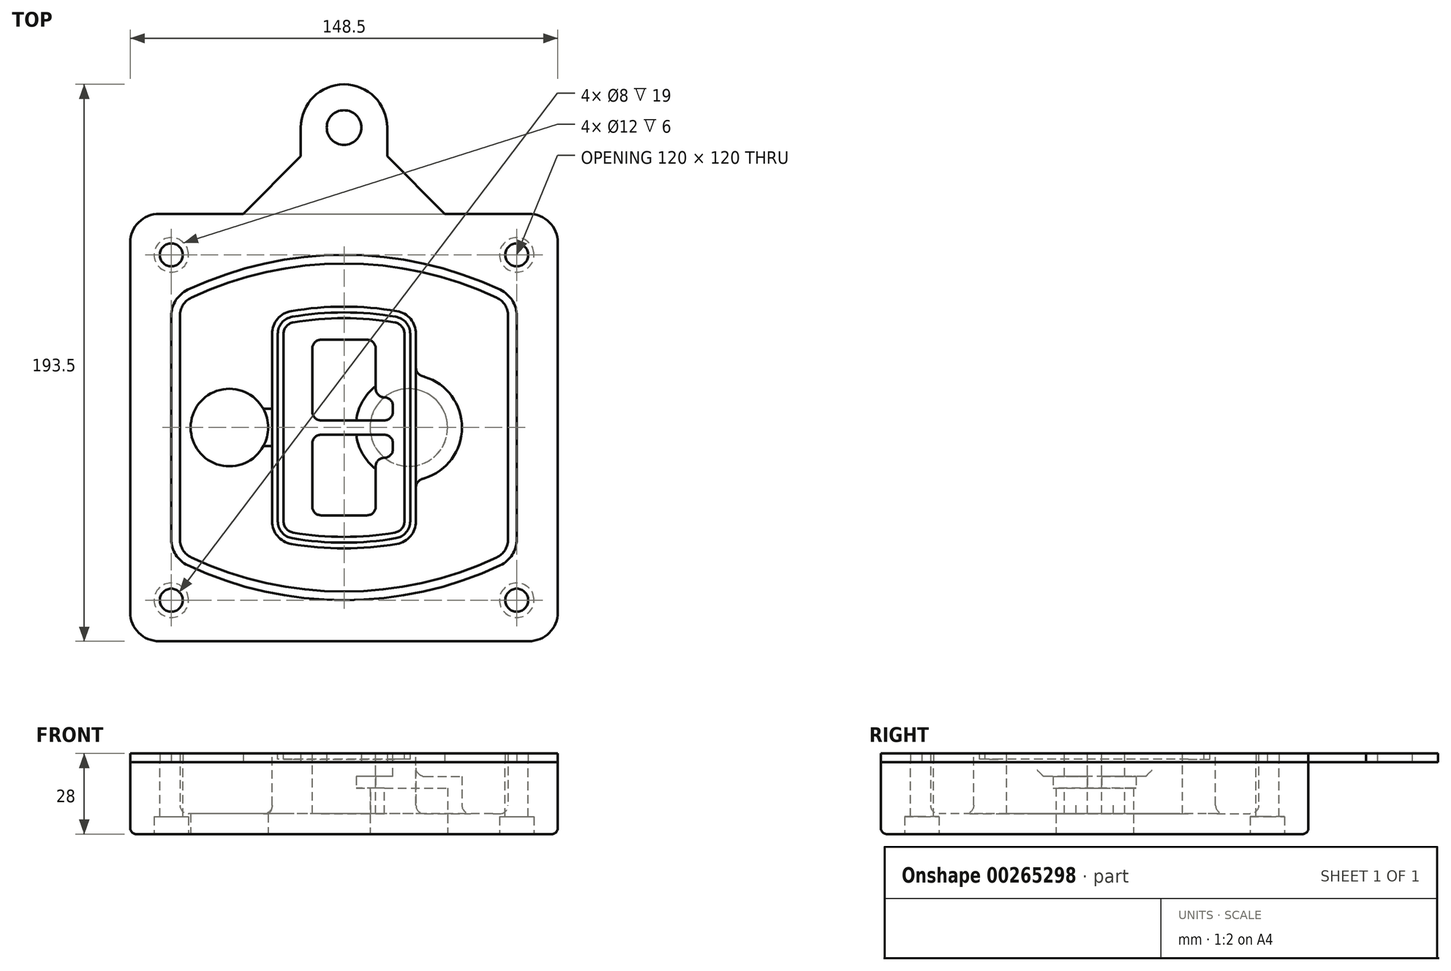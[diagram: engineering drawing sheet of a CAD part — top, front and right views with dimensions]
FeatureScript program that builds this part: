
annotation { "Feature Type Name" : "Feature", "Feature Type Description" : "" }
export const myFeature = defineFeature(function(context is Context, id is Id, definition is map)
    precondition{}
    {
        {
            var Q0;
            Q0=qCreatedBy(makeId("Top.planeOp"),FACE);
            var sketch = newSketch(context, id + "F0", { "sketchPlane" : qUnion([Q0])});
            skPoint(sketch, "E0.rect.middle", {"position": v(0, 0) * mm});
            skLineSegment(sketch, "E1.bottom", {"start": v(-64.25, -74.25) * mm, "end": v(64.25, -74.25) * mm});
            skLineSegment(sketch, "E1.top", {"start": v(-64.25, 74.25) * mm, "end": v(64.25, 74.25) * mm});
            skLineSegment(sketch, "E1.left", {"start": v(-74.25, -64.25) * mm, "end": v(-74.25, 64.25) * mm});
            skLineSegment(sketch, "E1.right", {"start": v(74.25, -64.25) * mm, "end": v(74.25, 64.25) * mm});
            skLineSegment(sketch, "E2", {"start": v(-74.25, 74.25) * mm, "end": v(74.25, -74.25) * mm, "construction": true});
            skLineSegment(sketch, "E3", {"start": v(74.25, 74.25) * mm, "end": v(-74.25, -74.25) * mm, "construction": true});
            skCircle(sketch, "E4", {"center": v(-60, 60) * mm, "radius": 4 * mm});
            skCircle(sketch, "E5", {"center": v(60, 60) * mm, "radius": 4 * mm});
            skCircle(sketch, "E6", {"center": v(60, -60) * mm, "radius": 4 * mm});
            skCircle(sketch, "E7", {"center": v(-60, -60) * mm, "radius": 4 * mm});
            skLineSegment(sketch, "E8", {"start": v(-60, 60) * mm, "end": v(60, 60) * mm, "construction": true});
            skLineSegment(sketch, "E9", {"start": v(60, 60) * mm, "end": v(60, -60) * mm, "construction": true});
            skLineSegment(sketch, "E10", {"start": v(60, -60) * mm, "end": v(-60, -60) * mm, "construction": true});
            skLineSegment(sketch, "E11", {"start": v(-60, -60) * mm, "end": v(-60, 60) * mm, "construction": true});
            skLineSegment(sketch, "E12", {"start": v(-60, 38.83) * mm, "end": v(-60, -38.83) * mm});
            skLineSegment(sketch, "E13", {"start": v(60, 38.83) * mm, "end": v(60, -38.83) * mm});
            skArc(sketch, "E14", {"start": v(54.26, 47.88) * mm, "mid": v(0, 60) * mm, "end": v(-54.26, 47.88) * mm});
            skArc(sketch, "E15", {"start": v(-54.26, -47.88) * mm, "mid": v(0, -60) * mm, "end": v(54.26, -47.88) * mm});
            skLineSegment(sketch, "E16", {"start": v(-60, 0) * mm, "end": v(60, 0) * mm, "construction": true});
            skPoint(sketch, "E17.visualSharp", {"position": v(-60, -45) * mm});
            skArc(sketch, "E17.filletArc", {"start": v(-60, -38.83) * mm, "mid": v(-58.44, -44.2) * mm, "end": v(-54.26, -47.88) * mm});
            skPoint(sketch, "E18.visualSharp", {"position": v(-60, 45) * mm});
            skArc(sketch, "E18.filletArc", {"start": v(-54.26, 47.88) * mm, "mid": v(-58.44, 44.2) * mm, "end": v(-60, 38.83) * mm});
            skPoint(sketch, "E19.visualSharp", {"position": v(60, 45) * mm});
            skArc(sketch, "E19.filletArc", {"start": v(60, 38.83) * mm, "mid": v(58.44, 44.2) * mm, "end": v(54.26, 47.88) * mm});
            skPoint(sketch, "E20.visualSharp", {"position": v(60, -45) * mm});
            skArc(sketch, "E20.filletArc", {"start": v(54.26, -47.88) * mm, "mid": v(58.44, -44.2) * mm, "end": v(60, -38.83) * mm});
            skPoint(sketch, "E21.visualSharp", {"position": v(-74.25, 74.25) * mm});
            skArc(sketch, "E21.filletArc", {"start": v(-64.25, 74.25) * mm, "mid": v(-71.32, 71.32) * mm, "end": v(-74.25, 64.25) * mm});
            skPoint(sketch, "E22.visualSharp", {"position": v(74.25, 74.25) * mm});
            skArc(sketch, "E22.filletArc", {"start": v(74.25, 64.25) * mm, "mid": v(71.32, 71.32) * mm, "end": v(64.25, 74.25) * mm});
            skPoint(sketch, "E23.visualSharp", {"position": v(74.25, -74.25) * mm});
            skArc(sketch, "E23.filletArc", {"start": v(64.25, -74.25) * mm, "mid": v(71.32, -71.32) * mm, "end": v(74.25, -64.25) * mm});
            skPoint(sketch, "E24.visualSharp", {"position": v(-74.25, -74.25) * mm});
            skArc(sketch, "E24.filletArc", {"start": v(-74.25, -64.25) * mm, "mid": v(-71.32, -71.32) * mm, "end": v(-64.25, -74.25) * mm});
            skArc(sketch, "E25.0", {"start": v(57, 38.83) * mm, "mid": v(55.9, 42.58) * mm, "end": v(52.98, 45.17) * mm});
            skLineSegment(sketch, "E25.1", {"start": v(57, 38.83) * mm, "end": v(57, -38.83) * mm});
            skArc(sketch, "E25.2", {"start": v(52.98, -45.17) * mm, "mid": v(55.9, -42.58) * mm, "end": v(57, -38.83) * mm});
            skArc(sketch, "E25.3", {"start": v(-52.98, -45.17) * mm, "mid": v(0, -57) * mm, "end": v(52.98, -45.17) * mm});
            skArc(sketch, "E25.4", {"start": v(-57, -38.83) * mm, "mid": v(-55.9, -42.58) * mm, "end": v(-52.98, -45.17) * mm});
            skArc(sketch, "E25.5", {"start": v(52.98, 45.17) * mm, "mid": v(0, 57) * mm, "end": v(-52.98, 45.17) * mm});
            skLineSegment(sketch, "E25.6", {"start": v(-57, 38.83) * mm, "end": v(-57, -38.83) * mm});
            skArc(sketch, "E25.7", {"start": v(-52.98, 45.17) * mm, "mid": v(-55.9, 42.58) * mm, "end": v(-57, 38.83) * mm});
            skArc(sketch, "E26.0", {"start": v(-55.96, 51.5) * mm, "mid": v(-61.82, 46.33) * mm, "end": v(-64, 38.83) * mm});
            skArc(sketch, "E26.1", {"start": v(55.96, 51.5) * mm, "mid": v(0, 64) * mm, "end": v(-55.96, 51.5) * mm});
            skArc(sketch, "E26.2", {"start": v(64, 38.83) * mm, "mid": v(61.82, 46.33) * mm, "end": v(55.96, 51.5) * mm});
            skLineSegment(sketch, "E26.3", {"start": v(64, 38.83) * mm, "end": v(64, -38.83) * mm});
            skArc(sketch, "E26.4", {"start": v(55.96, -51.5) * mm, "mid": v(61.82, -46.33) * mm, "end": v(64, -38.83) * mm});
            skLineSegment(sketch, "E26.5", {"start": v(-64, 38.83) * mm, "end": v(-64, -38.83) * mm});
            skArc(sketch, "E26.6", {"start": v(-55.96, -51.5) * mm, "mid": v(0, -64) * mm, "end": v(55.96, -51.5) * mm});
            skArc(sketch, "E26.7", {"start": v(-64, -38.83) * mm, "mid": v(-61.82, -46.33) * mm, "end": v(-55.96, -51.5) * mm});
            skSolve(sketch);
        }
        {
            var Q0;
            Q0=makeQuery(id+"F0.imprint","IMPRINT",FACE,{"disambiguationData":[TD([[makeQuery(id+"F0.imprint","IMPRINT",EDGE,{"derivedFrom":sQuery(id+"F0.wireOp",EDGE,"E1.bottom")}),1.0]])]});
            var Q1;
            Q1=makeQuery(id+"F0.imprint","IMPRINT",FACE,{"disambiguationData":[TD([[makeQuery(id+"F0.imprint","IMPRINT",EDGE,{"derivedFrom":sQuery(id+"F0.wireOp",EDGE,"E12")}),1.0]])]});
            var Q2;
            Q2=makeQuery(id+"F0.imprint","IMPRINT",FACE,{"disambiguationData":[TD([[makeQuery(id+"F0.imprint","IMPRINT",EDGE,{"derivedFrom":sQuery(id+"F0.wireOp",EDGE,"E25.0")}),1.0]])]});
            var Q3;
            Q3=makeQuery(id+"F0.imprint","IMPRINT",FACE,{"disambiguationData":[TD([[makeQuery(id+"F0.imprint","IMPRINT",EDGE,{"derivedFrom":sQuery(id+"F0.wireOp",EDGE,"E12")}),-1.0]])]});
            extrude(context, id + "F1", {"entities" : qUnion([Q0, Q1, Q2, Q3]), "oppositeDirection" : true, "depth" : 25 * mm});
        }
        {
            var Q0;
            Q0=makeQuery(id+"F0.imprint","IMPRINT",FACE,{"disambiguationData":[TD([[makeQuery(id+"F0.imprint","IMPRINT",EDGE,{"derivedFrom":sQuery(id+"F0.wireOp",EDGE,"E12")}),1.0]])]});
            extrude(context, id + "F2", {"entities" : qUnion([Q0]), "operationType" : NewBodyOperationType.ADD, "depth" : 3 * mm});
        }
        {
            var Q0;
            Q0=makeQuery(id+"F0.imprint","IMPRINT",FACE,{"disambiguationData":[TD([[makeQuery(id+"F0.imprint","IMPRINT",EDGE,{"derivedFrom":sQuery(id+"F0.wireOp",EDGE,"E25.0")}),1.0]])]});
            extrude(context, id + "F3", {"entities" : qUnion([Q0]), "operationType" : NewBodyOperationType.REMOVE, "oppositeDirection" : true, "depth" : 18 * mm});
        }
        {
            var Q0;
            Q0=makeQuery(id+"F2.opExtrude","CAP_FACE",FACE,{"disambiguationData":[OSD([sQuery(id+"F0.wireOp",EDGE,"E12"),sQuery(id+"F0.wireOp",EDGE,"E13"),sQuery(id+"F0.wireOp",EDGE,"E14"),sQuery(id+"F0.wireOp",EDGE,"E15"),sQuery(id+"F0.wireOp",EDGE,"E17.filletArc"),sQuery(id+"F0.wireOp",EDGE,"E18.filletArc"),sQuery(id+"F0.wireOp",EDGE,"E19.filletArc"),sQuery(id+"F0.wireOp",EDGE,"E20.filletArc"),sQuery(id+"F0.wireOp",EDGE,"E25.0"),sQuery(id+"F0.wireOp",EDGE,"E25.1"),sQuery(id+"F0.wireOp",EDGE,"E25.2"),sQuery(id+"F0.wireOp",EDGE,"E25.3"),sQuery(id+"F0.wireOp",EDGE,"E25.4"),sQuery(id+"F0.wireOp",EDGE,"E25.5"),sQuery(id+"F0.wireOp",EDGE,"E25.6"),sQuery(id+"F0.wireOp",EDGE,"E25.7")])],"isStart":false});
            var sketch = newSketch(context, id + "F4", { "sketchPlane" : qUnion([Q0])});
            skArc(sketch, "E27.0", {"start": v(-18.34, -40.45) * mm, "mid": v(0, -42) * mm, "end": v(18.34, -40.45) * mm});
            skArc(sketch, "E28.0", {"start": v(18.34, 40.45) * mm, "mid": v(0, 42) * mm, "end": v(-18.34, 40.45) * mm});
            skLineSegment(sketch, "E29", {"start": v(-25, 32.57) * mm, "end": v(-25, -32.57) * mm});
            skLineSegment(sketch, "E30", {"start": v(25, 32.57) * mm, "end": v(25, -32.57) * mm});
            skLineSegment(sketch, "E31", {"start": v(-25, 39.1) * mm, "end": v(25, 39.1) * mm, "construction": true});
            skLineSegment(sketch, "E32", {"start": v(-25, -39.1) * mm, "end": v(25, -39.1) * mm, "construction": true});
            skPoint(sketch, "E33.visualSharp", {"position": v(-25, 39.1) * mm});
            skArc(sketch, "E33.filletArc", {"start": v(-18.34, 40.45) * mm, "mid": v(-23.11, 37.73) * mm, "end": v(-25, 32.57) * mm});
            skPoint(sketch, "E34.visualSharp", {"position": v(25, 39.1) * mm});
            skArc(sketch, "E34.filletArc", {"start": v(25, 32.57) * mm, "mid": v(23.11, 37.73) * mm, "end": v(18.34, 40.45) * mm});
            skPoint(sketch, "E35.visualSharp", {"position": v(25, -39.1) * mm});
            skArc(sketch, "E35.filletArc", {"start": v(18.34, -40.45) * mm, "mid": v(23.11, -37.73) * mm, "end": v(25, -32.57) * mm});
            skPoint(sketch, "E36.visualSharp", {"position": v(-25, -39.1) * mm});
            skArc(sketch, "E36.filletArc", {"start": v(-25, -32.57) * mm, "mid": v(-23.11, -37.73) * mm, "end": v(-18.34, -40.45) * mm});
            skArc(sketch, "E37.0", {"start": v(52.98, 45.17) * mm, "mid": v(0, 57) * mm, "end": v(-52.98, 45.17) * mm});
            skArc(sketch, "E37.1", {"start": v(-52.98, 45.17) * mm, "mid": v(-55.9, 42.58) * mm, "end": v(-57, 38.83) * mm});
            skLineSegment(sketch, "E37.2", {"start": v(-57, 38.83) * mm, "end": v(-57, -38.83) * mm});
            skArc(sketch, "E37.3", {"start": v(-57, -38.83) * mm, "mid": v(-55.9, -42.58) * mm, "end": v(-52.98, -45.17) * mm});
            skArc(sketch, "E37.4", {"start": v(-52.98, -45.17) * mm, "mid": v(0, -57) * mm, "end": v(52.98, -45.17) * mm});
            skArc(sketch, "E37.5", {"start": v(52.98, -45.17) * mm, "mid": v(55.9, -42.58) * mm, "end": v(57, -38.83) * mm});
            skLineSegment(sketch, "E37.6", {"start": v(57, 38.83) * mm, "end": v(57, -38.83) * mm});
            skArc(sketch, "E37.7", {"start": v(57, 38.83) * mm, "mid": v(55.9, 42.58) * mm, "end": v(52.98, 45.17) * mm});
            skLineSegment(sketch, "E38.0", {"start": v(23, 32.57) * mm, "end": v(23, -32.57) * mm});
            skArc(sketch, "E38.1", {"start": v(18, -38.48) * mm, "mid": v(21.58, -36.44) * mm, "end": v(23, -32.57) * mm});
            skArc(sketch, "E38.2", {"start": v(-18, -38.48) * mm, "mid": v(0, -40) * mm, "end": v(18, -38.48) * mm});
            skArc(sketch, "E38.3", {"start": v(-23, -32.57) * mm, "mid": v(-21.58, -36.44) * mm, "end": v(-18, -38.48) * mm});
            skLineSegment(sketch, "E38.4", {"start": v(-23, 32.57) * mm, "end": v(-23, -32.57) * mm});
            skArc(sketch, "E38.5", {"start": v(23, 32.57) * mm, "mid": v(21.58, 36.44) * mm, "end": v(18, 38.48) * mm});
            skArc(sketch, "E38.6", {"start": v(-18, 38.48) * mm, "mid": v(-21.58, 36.44) * mm, "end": v(-23, 32.57) * mm});
            skArc(sketch, "E38.7", {"start": v(18, 38.48) * mm, "mid": v(0, 40) * mm, "end": v(-18, 38.48) * mm});
            skArc(sketch, "E39.0", {"start": v(21, 32.57) * mm, "mid": v(20.06, 35.15) * mm, "end": v(17.67, 36.5) * mm});
            skLineSegment(sketch, "E39.1", {"start": v(21, 32.57) * mm, "end": v(21, -32.57) * mm});
            skArc(sketch, "E39.2", {"start": v(17.67, -36.5) * mm, "mid": v(20.06, -35.15) * mm, "end": v(21, -32.57) * mm});
            skArc(sketch, "E39.3", {"start": v(-17.67, -36.5) * mm, "mid": v(0, -38) * mm, "end": v(17.67, -36.5) * mm});
            skArc(sketch, "E39.4", {"start": v(-21, -32.57) * mm, "mid": v(-20.06, -35.15) * mm, "end": v(-17.67, -36.5) * mm});
            skArc(sketch, "E39.5", {"start": v(17.67, 36.5) * mm, "mid": v(0, 38) * mm, "end": v(-17.67, 36.5) * mm});
            skLineSegment(sketch, "E39.6", {"start": v(-21, 32.57) * mm, "end": v(-21, -32.57) * mm});
            skArc(sketch, "E39.7", {"start": v(-17.67, 36.5) * mm, "mid": v(-20.06, 35.15) * mm, "end": v(-21, 32.57) * mm});
            skLineSegment(sketch, "E40", {"start": v(-25, 0) * mm, "end": v(25, 0) * mm, "construction": true});
            skLineSegment(sketch, "E41", {"start": v(-11, 5.5) * mm, "end": v(-11, 27.5) * mm});
            skLineSegment(sketch, "E42", {"start": v(-8, 30.5) * mm, "end": v(8, 30.5) * mm});
            skLineSegment(sketch, "E43", {"start": v(11, 27.5) * mm, "end": v(11, 13.5) * mm});
            skLineSegment(sketch, "E44", {"start": v(14, 10.5) * mm, "end": v(14, 10.5) * mm});
            skLineSegment(sketch, "E45", {"start": v(17, 7.5) * mm, "end": v(17, 5.5) * mm});
            skLineSegment(sketch, "E46", {"start": v(14, 2.5) * mm, "end": v(-8, 2.5) * mm});
            skPoint(sketch, "E47.visualSharp", {"position": v(-11, 30.5) * mm});
            skArc(sketch, "E47.filletArc", {"start": v(-8, 30.5) * mm, "mid": v(-10.12, 29.62) * mm, "end": v(-11, 27.5) * mm});
            skPoint(sketch, "E48.visualSharp", {"position": v(11, 30.5) * mm});
            skArc(sketch, "E48.filletArc", {"start": v(11, 27.5) * mm, "mid": v(10.12, 29.62) * mm, "end": v(8, 30.5) * mm});
            skPoint(sketch, "E49.visualSharp", {"position": v(11, 10.5) * mm});
            skArc(sketch, "E49.filletArc", {"start": v(11, 13.5) * mm, "mid": v(11.88, 11.38) * mm, "end": v(14, 10.5) * mm});
            skPoint(sketch, "E50.visualSharp", {"position": v(17, 10.5) * mm});
            skArc(sketch, "E50.filletArc", {"start": v(17, 7.5) * mm, "mid": v(16.12, 9.62) * mm, "end": v(14, 10.5) * mm});
            skPoint(sketch, "E51.visualSharp", {"position": v(17, 2.5) * mm});
            skArc(sketch, "E51.filletArc", {"start": v(14, 2.5) * mm, "mid": v(16.12, 3.38) * mm, "end": v(17, 5.5) * mm});
            skPoint(sketch, "E52.visualSharp", {"position": v(-11, 2.5) * mm});
            skArc(sketch, "E52.filletArc", {"start": v(-11, 5.5) * mm, "mid": v(-10.12, 3.38) * mm, "end": v(-8, 2.5) * mm});
            skLineSegment(sketch, "E53.0.MirrorCS", {"start": v(14, -2.5) * mm, "end": v(-8, -2.5) * mm});
            skArc(sketch, "E54.0.MirrorCS", {"start": v(-11, -5.5) * mm, "mid": v(-10.12, -3.38) * mm, "end": v(-8, -2.5) * mm});
            skLineSegment(sketch, "E55.0.MirrorCS", {"start": v(-11, -5.5) * mm, "end": v(-11, -27.5) * mm});
            skArc(sketch, "E56.0.MirrorCS", {"start": v(-8, -30.5) * mm, "mid": v(-10.12, -29.62) * mm, "end": v(-11, -27.5) * mm});
            skLineSegment(sketch, "E57.0.MirrorCS", {"start": v(-8, -30.5) * mm, "end": v(8, -30.5) * mm});
            skArc(sketch, "E58.0.MirrorCS", {"start": v(11, -27.5) * mm, "mid": v(10.12, -29.62) * mm, "end": v(8, -30.5) * mm});
            skLineSegment(sketch, "E59.0.MirrorCS", {"start": v(11, -27.5) * mm, "end": v(11, -13.5) * mm});
            skArc(sketch, "E60.0.MirrorCS", {"start": v(11, -13.5) * mm, "mid": v(11.88, -11.38) * mm, "end": v(14, -10.5) * mm});
            skArc(sketch, "E61.0.MirrorCS", {"start": v(17, -7.5) * mm, "mid": v(16.12, -9.62) * mm, "end": v(14, -10.5) * mm});
            skLineSegment(sketch, "E62.0.MirrorCS", {"start": v(17, -7.5) * mm, "end": v(17, -5.5) * mm});
            skArc(sketch, "E63.0.MirrorCS", {"start": v(14, -2.5) * mm, "mid": v(16.12, -3.38) * mm, "end": v(17, -5.5) * mm});
            skSolve(sketch);
        }
        {
            var Q0;
            Q0=makeQuery(id+"F4.imprint","IMPRINT",FACE,{"disambiguationData":[TD([[makeQuery(id+"F4.imprint","IMPRINT",EDGE,{"derivedFrom":sQuery(id+"F4.wireOp",EDGE,"E27.0")}),1.0]])]});
            var Q1;
            Q1=makeQuery(id+"F4.imprint","IMPRINT",FACE,{"disambiguationData":[TD([[makeQuery(id+"F4.imprint","IMPRINT",EDGE,{"derivedFrom":sQuery(id+"F4.wireOp",EDGE,"E38.0")}),-1.0]])]});
            var Q2;
            Q2=makeQuery(id+"F4.imprint","IMPRINT",FACE,{"disambiguationData":[TD([[makeQuery(id+"F4.imprint","IMPRINT",EDGE,{"derivedFrom":sQuery(id+"F4.wireOp",EDGE,"E39.0")}),1.0]])]});
            extrude(context, id + "F5", {"entities" : qUnion([Q0, Q1, Q2]), "operationType" : NewBodyOperationType.ADD, "endBound" : BoundingType.UP_TO_NEXT, "oppositeDirection" : true, "depth" : 25 * mm});
        }
        {
            var Q0;
            Q0=makeQuery(id+"F4.imprint","IMPRINT",FACE,{"disambiguationData":[TD([[makeQuery(id+"F4.imprint","IMPRINT",EDGE,{"derivedFrom":sQuery(id+"F4.wireOp",EDGE,"E38.0")}),-1.0]])]});
            extrude(context, id + "F6", {"entities" : qUnion([Q0]), "operationType" : NewBodyOperationType.REMOVE, "oppositeDirection" : true, "depth" : 2 * mm});
        }
        {
            var Q0;
            Q0=makeQuery(id+"F1.opExtrude","CAP_FACE",FACE,{"disambiguationData":[OSD([sQuery(id+"F0.wireOp",EDGE,"E1.bottom"),sQuery(id+"F0.wireOp",EDGE,"E1.top"),sQuery(id+"F0.wireOp",EDGE,"E1.left"),sQuery(id+"F0.wireOp",EDGE,"E1.right"),sQuery(id+"F0.wireOp",EDGE,"E4"),sQuery(id+"F0.wireOp",EDGE,"E5"),sQuery(id+"F0.wireOp",EDGE,"E6"),sQuery(id+"F0.wireOp",EDGE,"E7"),sQuery(id+"F0.wireOp",EDGE,"E21.filletArc"),sQuery(id+"F0.wireOp",EDGE,"E22.filletArc"),sQuery(id+"F0.wireOp",EDGE,"E23.filletArc"),sQuery(id+"F0.wireOp",EDGE,"E24.filletArc")])],"isStart":false});
            var sketch = newSketch(context, id + "F7", { "sketchPlane" : qUnion([Q0])});
            skCircle(sketch, "E64", {"center": v(22.5, 0) * mm, "radius": 13.47 * mm});
            skCircle(sketch, "E65", {"center": v(-39.81, 0) * mm, "radius": 13.47 * mm});
            skLineSegment(sketch, "E66", {"start": v(74.25, 0) * mm, "end": v(-74.25, 0) * mm});
            skCircle(sketch, "E67", {"center": v(22.5, 0) * mm, "radius": 18.47 * mm});
            skCircle(sketch, "E68", {"center": v(60, -60) * mm, "radius": 6 * mm});
            skCircle(sketch, "E69", {"center": v(-60, -60) * mm, "radius": 6 * mm});
            skCircle(sketch, "E70", {"center": v(-60, 60) * mm, "radius": 6 * mm});
            skCircle(sketch, "E71", {"center": v(60, 60) * mm, "radius": 6 * mm});
            skSolve(sketch);
        }
        {
            var Q0;
            {var subQ1=sQuery(id+"F7.wireOp",EDGE,"E66");var subQ4=sQuery(id+"F7.wireOp",EDGE,"E64");var subQ6=makeQuery(id+"F7.imprint","INTERSECT",VERTEX,{"disambiguationData":[OD(0.0)],"derivedFrom":[subQ4,subQ1]});Q0=makeQuery(id+"F7.imprint","IMPRINT",FACE,{"disambiguationData":[TD([[makeQuery(id+"F7.imprint","IMPRINT",EDGE,{"disambiguationData":[TD([[subQ6,-1.0]])],"derivedFrom":subQ4}),-1.0]])]});}
            var Q1;
            {var subQ0=sQuery(id+"F7.wireOp",EDGE,"E66");var subQ1=sQuery(id+"F7.wireOp",EDGE,"E64");var subQ3=makeQuery(id+"F7.imprint","INTERSECT",VERTEX,{"disambiguationData":[OD(0.0)],"derivedFrom":[subQ1,subQ0]});Q1=makeQuery(id+"F7.imprint","IMPRINT",FACE,{"disambiguationData":[TD([[makeQuery(id+"F7.imprint","IMPRINT",EDGE,{"disambiguationData":[TD([[subQ3,-1.0]])],"derivedFrom":subQ1}),1.0]])]});}
            var Q2;
            {var subQ0=sQuery(id+"F7.wireOp",EDGE,"E66");var subQ1=sQuery(id+"F7.wireOp",EDGE,"E64");var subQ3=makeQuery(id+"F7.imprint","INTERSECT",VERTEX,{"disambiguationData":[OD(0.0)],"derivedFrom":[subQ1,subQ0]});Q2=makeQuery(id+"F7.imprint","IMPRINT",FACE,{"disambiguationData":[TD([[makeQuery(id+"F7.imprint","IMPRINT",EDGE,{"disambiguationData":[TD([[subQ3,1.0]])],"derivedFrom":subQ1}),1.0]])]});}
            var Q3;
            {var subQ1=sQuery(id+"F7.wireOp",EDGE,"E66");var subQ4=sQuery(id+"F7.wireOp",EDGE,"E64");var subQ6=makeQuery(id+"F7.imprint","INTERSECT",VERTEX,{"disambiguationData":[OD(0.0)],"derivedFrom":[subQ4,subQ1]});Q3=makeQuery(id+"F7.imprint","IMPRINT",FACE,{"disambiguationData":[TD([[makeQuery(id+"F7.imprint","IMPRINT",EDGE,{"disambiguationData":[TD([[subQ6,1.0]])],"derivedFrom":subQ4}),-1.0]])]});}
            extrude(context, id + "F8", {"entities" : qUnion([Q0, Q1, Q2, Q3]), "operationType" : NewBodyOperationType.ADD, "oppositeDirection" : true, "depth" : 20 * mm});
        }
        {
            var Q0;
            {var subQ0=sQuery(id+"F7.wireOp",EDGE,"E66");var subQ1=sQuery(id+"F7.wireOp",EDGE,"E64");var subQ3=makeQuery(id+"F7.imprint","INTERSECT",VERTEX,{"disambiguationData":[OD(0.0)],"derivedFrom":[subQ1,subQ0]});Q0=makeQuery(id+"F7.imprint","IMPRINT",FACE,{"disambiguationData":[TD([[makeQuery(id+"F7.imprint","IMPRINT",EDGE,{"disambiguationData":[TD([[subQ3,-1.0]])],"derivedFrom":subQ1}),1.0]])]});}
            var Q1;
            {var subQ0=sQuery(id+"F7.wireOp",EDGE,"E66");var subQ1=sQuery(id+"F7.wireOp",EDGE,"E64");var subQ3=makeQuery(id+"F7.imprint","INTERSECT",VERTEX,{"disambiguationData":[OD(0.0)],"derivedFrom":[subQ1,subQ0]});Q1=makeQuery(id+"F7.imprint","IMPRINT",FACE,{"disambiguationData":[TD([[makeQuery(id+"F7.imprint","IMPRINT",EDGE,{"disambiguationData":[TD([[subQ3,1.0]])],"derivedFrom":subQ1}),1.0]])]});}
            extrude(context, id + "F9", {"entities" : qUnion([Q0, Q1]), "operationType" : NewBodyOperationType.REMOVE, "oppositeDirection" : true, "depth" : 16 * mm});
        }
        {
            var Q0;
            {var subQ0=sQuery(id+"F7.wireOp",EDGE,"E66");var subQ1=sQuery(id+"F7.wireOp",EDGE,"E65");var subQ3=makeQuery(id+"F7.imprint","INTERSECT",VERTEX,{"disambiguationData":[OD(0.0)],"derivedFrom":[subQ1,subQ0]});Q0=makeQuery(id+"F7.imprint","IMPRINT",FACE,{"disambiguationData":[TD([[makeQuery(id+"F7.imprint","IMPRINT",EDGE,{"disambiguationData":[TD([[subQ3,-1.0]])],"derivedFrom":subQ1}),1.0]])]});}
            var Q1;
            {var subQ0=sQuery(id+"F7.wireOp",EDGE,"E66");var subQ1=sQuery(id+"F7.wireOp",EDGE,"E65");var subQ3=makeQuery(id+"F7.imprint","INTERSECT",VERTEX,{"disambiguationData":[OD(0.0)],"derivedFrom":[subQ1,subQ0]});Q1=makeQuery(id+"F7.imprint","IMPRINT",FACE,{"disambiguationData":[TD([[makeQuery(id+"F7.imprint","IMPRINT",EDGE,{"disambiguationData":[TD([[subQ3,1.0]])],"derivedFrom":subQ1}),1.0]])]});}
            extrude(context, id + "F10", {"entities" : qUnion([Q0, Q1]), "operationType" : NewBodyOperationType.REMOVE, "oppositeDirection" : true, "depth" : 25 * mm});
        }
        {
            var Q0;
            Q0=makeQuery(id+"F7.imprint","IMPRINT",FACE,{"disambiguationData":[TD([[makeQuery(id+"F7.imprint","IMPRINT",EDGE,{"derivedFrom":sQuery(id+"F7.wireOp",EDGE,"E68")}),1.0]])]});
            var Q1;
            Q1=makeQuery(id+"F7.imprint","IMPRINT",FACE,{"disambiguationData":[TD([[makeQuery(id+"F7.imprint","IMPRINT",EDGE,{"derivedFrom":makeQuery(id+"F1.opExtrude","CAP_EDGE",EDGE,{"disambiguationData":[OSD([sQuery(id+"F0.wireOp",EDGE,"E5")])],"isStart":false})}),-1.0]])]});
            var Q2;
            Q2=makeQuery(id+"F7.imprint","IMPRINT",FACE,{"disambiguationData":[TD([[makeQuery(id+"F7.imprint","IMPRINT",EDGE,{"derivedFrom":sQuery(id+"F7.wireOp",EDGE,"E69")}),1.0]])]});
            var Q3;
            Q3=makeQuery(id+"F7.imprint","IMPRINT",FACE,{"disambiguationData":[TD([[makeQuery(id+"F7.imprint","IMPRINT",EDGE,{"derivedFrom":makeQuery(id+"F1.opExtrude","CAP_EDGE",EDGE,{"disambiguationData":[OSD([sQuery(id+"F0.wireOp",EDGE,"E4")])],"isStart":false})}),-1.0]])]});
            var Q4;
            Q4=makeQuery(id+"F7.imprint","IMPRINT",FACE,{"disambiguationData":[TD([[makeQuery(id+"F7.imprint","IMPRINT",EDGE,{"derivedFrom":sQuery(id+"F7.wireOp",EDGE,"E70")}),1.0]])]});
            var Q5;
            Q5=makeQuery(id+"F7.imprint","IMPRINT",FACE,{"disambiguationData":[TD([[makeQuery(id+"F7.imprint","IMPRINT",EDGE,{"derivedFrom":makeQuery(id+"F1.opExtrude","CAP_EDGE",EDGE,{"disambiguationData":[OSD([sQuery(id+"F0.wireOp",EDGE,"E7")])],"isStart":false})}),-1.0]])]});
            var Q6;
            Q6=makeQuery(id+"F7.imprint","IMPRINT",FACE,{"disambiguationData":[TD([[makeQuery(id+"F7.imprint","IMPRINT",EDGE,{"derivedFrom":sQuery(id+"F7.wireOp",EDGE,"E71")}),1.0]])]});
            var Q7;
            Q7=makeQuery(id+"F7.imprint","IMPRINT",FACE,{"disambiguationData":[TD([[makeQuery(id+"F7.imprint","IMPRINT",EDGE,{"derivedFrom":makeQuery(id+"F1.opExtrude","CAP_EDGE",EDGE,{"disambiguationData":[OSD([sQuery(id+"F0.wireOp",EDGE,"E6")])],"isStart":false})}),-1.0]])]});
            extrude(context, id + "F11", {"entities" : qUnion([Q0, Q1, Q2, Q3, Q4, Q5, Q6, Q7]), "operationType" : NewBodyOperationType.REMOVE, "oppositeDirection" : true, "depth" : 6 * mm});
        }
        {
            var Q0;
            Q0=makeQuery(id+"F9.boolean.opBoolean","COPY",FACE,{"derivedFrom":makeQuery(id+"F9.opExtrude","CAP_FACE",FACE,{"disambiguationData":[OSD([sQuery(id+"F7.wireOp",EDGE,"E64")])],"isStart":false})});
            var sketch = newSketch(context, id + "F12", { "sketchPlane" : qUnion([Q0])});
            skArc(sketch, "E72.0", {"start": v(11, 14.45) * mm, "mid": v(6.45, 9.13) * mm, "end": v(4.2, 2.5) * mm});
            skArc(sketch, "E72.1", {"start": v(4.2, -2.5) * mm, "mid": v(6.45, -9.13) * mm, "end": v(11, -14.45) * mm});
            skLineSegment(sketch, "E73", {"start": v(4.2, -2.5) * mm, "end": v(14, -2.5) * mm});
            skLineSegment(sketch, "E74.0", {"start": v(14, 2.5) * mm, "end": v(4.2, 2.5) * mm});
            skArc(sketch, "E74.1", {"start": v(14, 2.5) * mm, "mid": v(16.12, 3.38) * mm, "end": v(17, 5.5) * mm});
            skLineSegment(sketch, "E74.2", {"start": v(17, 7.5) * mm, "end": v(17, 5.5) * mm});
            skArc(sketch, "E74.3", {"start": v(17, 7.5) * mm, "mid": v(16.12, 9.62) * mm, "end": v(14, 10.5) * mm});
            skArc(sketch, "E74.4", {"start": v(11, 13.5) * mm, "mid": v(11.88, 11.38) * mm, "end": v(14, 10.5) * mm});
            skLineSegment(sketch, "E74.5", {"start": v(11, 14.45) * mm, "end": v(11, 13.5) * mm});
            skLineSegment(sketch, "E74.7", {"start": v(14, -2.5) * mm, "end": v(4.2, -2.5) * mm});
            skArc(sketch, "E74.8", {"start": v(14, -2.5) * mm, "mid": v(16.12, -3.38) * mm, "end": v(17, -5.5) * mm});
            skLineSegment(sketch, "E74.9", {"start": v(17, -7.5) * mm, "end": v(17, -5.5) * mm});
            skArc(sketch, "E74.10", {"start": v(17, -7.5) * mm, "mid": v(16.12, -9.62) * mm, "end": v(14, -10.5) * mm});
            skArc(sketch, "E74.11", {"start": v(11, -13.5) * mm, "mid": v(11.88, -11.38) * mm, "end": v(14, -10.5) * mm});
            skLineSegment(sketch, "E74.12", {"start": v(11, -14.45) * mm, "end": v(11, -13.5) * mm});
            skPoint(sketch, "E75.orphan", {"position": v(11, -27.5) * mm});
            skPoint(sketch, "E76.orphan", {"position": v(-8, -2.5) * mm});
            skPoint(sketch, "E77.orphan", {"position": v(-8, 2.5) * mm});
            skPoint(sketch, "E78.orphan", {"position": v(11, 27.5) * mm});
            skSolve(sketch);
        }
        {
            var Q0;
            {var subQ7=sQuery(id+"F12.wireOp",EDGE,"E72.0");var subQ14=sQuery(id+"F12.wireOp",EDGE,"E72.1");var subQ16=sQuery(id+"F12.wireOp",EDGE,"E74.1");var subQ18=sQuery(id+"F12.wireOp",EDGE,"E74.8");Q0=qUnion([makeQuery(id+"F12.imprint","IMPRINT",FACE,{"disambiguationData":[TD([[makeQuery(id+"F12.imprint","IMPRINT",EDGE,{"derivedFrom":subQ7}),1.0]])]}),makeQuery(id+"F12.imprint","IMPRINT",FACE,{"disambiguationData":[TD([[makeQuery(id+"F12.imprint","IMPRINT",EDGE,{"derivedFrom":subQ14}),1.0]])]}),makeQuery(id+"F12.imprint","IMPRINT",FACE,{"disambiguationData":[TD([[makeQuery(id+"F12.imprint","IMPRINT",EDGE,{"derivedFrom":subQ16}),1.0]])]}),makeQuery(id+"F12.imprint","IMPRINT",FACE,{"disambiguationData":[TD([[makeQuery(id+"F12.imprint","IMPRINT",EDGE,{"derivedFrom":subQ18}),-1.0]])]})]);}
            var Q1;
            Q1=makeQuery(id+"F5.boolean.opBoolean","SPLIT",FACE,{"disambiguationData":[TD([makeQuery(id+"F5.opExtrude","SWEPT_FACE",FACE,{"disambiguationData":[OSD([sQuery(id+"F4.wireOp",EDGE,"E41")])]})])],"derivedFrom":makeQuery(id+"F3.boolean.opBoolean","COPY",FACE,{"derivedFrom":makeQuery(id+"F3.opExtrude","CAP_FACE",FACE,{"disambiguationData":[OSD([sQuery(id+"F0.wireOp",EDGE,"E25.0"),sQuery(id+"F0.wireOp",EDGE,"E25.1"),sQuery(id+"F0.wireOp",EDGE,"E25.2"),sQuery(id+"F0.wireOp",EDGE,"E25.3"),sQuery(id+"F0.wireOp",EDGE,"E25.4"),sQuery(id+"F0.wireOp",EDGE,"E25.5"),sQuery(id+"F0.wireOp",EDGE,"E25.6"),sQuery(id+"F0.wireOp",EDGE,"E25.7")])],"isStart":false})})});
            extrude(context, id + "F13", {"entities" : qUnion([Q0]), "operationType" : NewBodyOperationType.REMOVE, "endBound" : BoundingType.UP_TO_SURFACE, "endBoundEntityFace" : qUnion([Q1]), "depth" : 25 * mm});
        }
        {
            var Q0;
            Q0=makeQuery(id+"F3.boolean.opBoolean","COPY",EDGE,{"derivedFrom":makeQuery(id+"F3.opExtrude","CAP_EDGE",EDGE,{"disambiguationData":[OSD([sQuery(id+"F0.wireOp",EDGE,"E25.6")])],"isStart":false})});
            var Q1;
            Q1=makeQuery(id+"F8.boolean.opBoolean","INTERSECT",EDGE,{"derivedFrom":[makeQuery(id+"F5.opExtrude","SWEPT_FACE",FACE,{"disambiguationData":[OSD([sQuery(id+"F4.wireOp",EDGE,"E30")])]}),makeQuery(id+"F8.opExtrude","CAP_FACE",FACE,{"disambiguationData":[OSD([sQuery(id+"F7.wireOp",EDGE,"E67")])],"isStart":false})]});
            var Q2;
            Q2=makeQuery(id+"F8.boolean.opBoolean","INTERSECT",EDGE,{"disambiguationData":[OD(1.0)],"derivedFrom":[makeQuery(id+"F5.opExtrude","SWEPT_FACE",FACE,{"disambiguationData":[OSD([sQuery(id+"F4.wireOp",EDGE,"E30")])]}),makeQuery(id+"F8.opExtrude","SWEPT_FACE",FACE,{"disambiguationData":[OSD([sQuery(id+"F7.wireOp",EDGE,"E67")])]})]});
            var Q3;
            {var subQ0=sQuery(id+"F4.wireOp",EDGE,"E30");Q3=makeQuery(id+"F8.boolean.opBoolean","SPLIT",EDGE,{"disambiguationData":[TD([makeQuery(id+"F5.opExtrude","SWEPT_FACE",FACE,{"disambiguationData":[OSD([sQuery(id+"F4.wireOp",EDGE,"E35.filletArc")])]})])],"derivedFrom":makeQuery(id+"F5.opExtrude","CAP_EDGE",EDGE,{"disambiguationData":[OSD([subQ0])],"isStart":false})});}
            var Q4;
            {var subQ0=sQuery(id+"F0.wireOp",EDGE,"E25.7");var subQ1=sQuery(id+"F0.wireOp",EDGE,"E25.1");var subQ2=sQuery(id+"F0.wireOp",EDGE,"E25.6");var subQ3=sQuery(id+"F0.wireOp",EDGE,"E25.5");var subQ4=sQuery(id+"F0.wireOp",EDGE,"E25.4");var subQ5=sQuery(id+"F0.wireOp",EDGE,"E25.0");var subQ6=sQuery(id+"F0.wireOp",EDGE,"E25.2");var subQ7=sQuery(id+"F0.wireOp",EDGE,"E25.3");Q4=makeQuery(id+"F8.boolean.opBoolean","INTERSECT",EDGE,{"derivedFrom":[makeQuery(id+"F5.boolean.opBoolean","SPLIT",FACE,{"disambiguationData":[TD([makeQuery(id+"F2.opExtrude","SWEPT_FACE",FACE,{"disambiguationData":[OSD([subQ5])]})])],"derivedFrom":makeQuery(id+"F3.boolean.opBoolean","COPY",FACE,{"derivedFrom":makeQuery(id+"F3.opExtrude","CAP_FACE",FACE,{"disambiguationData":[OSD([subQ5,subQ1,subQ6,subQ7,subQ4,subQ3,subQ2,subQ0])],"isStart":false})})}),makeQuery(id+"F8.opExtrude","SWEPT_FACE",FACE,{"disambiguationData":[OSD([sQuery(id+"F7.wireOp",EDGE,"E67")])]})]});}
            var Q5;
            Q5=makeQuery(id+"F8.boolean.opBoolean","INTERSECT",EDGE,{"disambiguationData":[OD(0.0)],"derivedFrom":[makeQuery(id+"F5.opExtrude","SWEPT_FACE",FACE,{"disambiguationData":[OSD([sQuery(id+"F4.wireOp",EDGE,"E30")])]}),makeQuery(id+"F8.opExtrude","SWEPT_FACE",FACE,{"disambiguationData":[OSD([sQuery(id+"F7.wireOp",EDGE,"E67")])]})]});
            fillet(context, id + "F14", {"entities" : qUnion([Q0, Q1, Q2, Q3, Q4, Q5]), "radius" : 3 * mm, "tangentPropagation" : true, "allowEdgeOverflow" : false});
        }
        {
            var Q0;
            Q0=makeQuery(id+"F1.opExtrude","CAP_EDGE",EDGE,{"disambiguationData":[OSD([sQuery(id+"F0.wireOp",EDGE,"E1.bottom")])],"isStart":false});
            fillet(context, id + "F15", {"entities" : qUnion([Q0]), "radius" : 2 * mm, "tangentPropagation" : true, "allowEdgeOverflow" : false});
        }
        {
            var Q0;
            {var subQ0=sQuery(id+"F0.wireOp",EDGE,"E22.filletArc");var subQ1=sQuery(id+"F0.wireOp",EDGE,"E7");var subQ2=sQuery(id+"F0.wireOp",EDGE,"E6");var subQ3=sQuery(id+"F0.wireOp",EDGE,"E5");var subQ4=sQuery(id+"F0.wireOp",EDGE,"E4");var subQ5=sQuery(id+"F0.wireOp",EDGE,"E1.bottom");var subQ6=sQuery(id+"F0.wireOp",EDGE,"E21.filletArc");var subQ7=sQuery(id+"F0.wireOp",EDGE,"E1.top");var subQ8=sQuery(id+"F0.wireOp",EDGE,"E1.left");var subQ9=sQuery(id+"F0.wireOp",EDGE,"E1.right");var subQ10=sQuery(id+"F0.wireOp",EDGE,"E23.filletArc");var subQ11=sQuery(id+"F0.wireOp",EDGE,"E24.filletArc");Q0=makeQuery(id+"F2.boolean.opBoolean","SPLIT",FACE,{"disambiguationData":[TD([makeQuery(id+"F1.opExtrude","SWEPT_FACE",FACE,{"disambiguationData":[OSD([subQ5])]})])],"derivedFrom":makeQuery(id+"F1.opExtrude","CAP_FACE",FACE,{"disambiguationData":[OSD([subQ5,subQ7,subQ8,subQ9,subQ4,subQ3,subQ2,subQ1,subQ6,subQ0,subQ10,subQ11])],"isStart":true})});}
            var sketch = newSketch(context, id + "F16", { "sketchPlane" : qUnion([Q0])});
            skLineSegment(sketch, "E79", {"start": v(0, 74.25) * mm, "end": v(35, 74.25) * mm});
            skLineSegment(sketch, "E80", {"start": v(0, 74.25) * mm, "end": v(-35, 74.25) * mm});
            skLineSegment(sketch, "E81", {"start": v(-35, 74.25) * mm, "end": v(-15, 94.25) * mm});
            skLineSegment(sketch, "E82", {"start": v(35, 74.25) * mm, "end": v(15, 94.25) * mm});
            skLineSegment(sketch, "E83", {"start": v(15, 104.25) * mm, "end": v(15, 94.25) * mm});
            skLineSegment(sketch, "E84", {"start": v(-15, 94.25) * mm, "end": v(-15, 104.25) * mm});
            skArc(sketch, "E85", {"start": v(15, 104.25) * mm, "mid": v(0, 119.25) * mm, "end": v(-15, 104.25) * mm});
            skCircle(sketch, "E86", {"center": v(0, 104.25) * mm, "radius": 6 * mm});
            skLineSegment(sketch, "E87", {"start": v(0, 104.25) * mm, "end": v(0, 74.25) * mm, "construction": true});
            skLineSegment(sketch, "E88", {"start": v(-74.25, 0) * mm, "end": v(74.25, 0) * mm, "construction": true});
            skArc(sketch, "E89.MirrorCS", {"start": v(15, -104.25) * mm, "mid": v(0, -119.25) * mm, "end": v(-15, -104.25) * mm});
            skCircle(sketch, "E90.MirrorC", {"center": v(0, -104.25) * mm, "radius": 6 * mm});
            skLineSegment(sketch, "E91.MirrorCS", {"start": v(-15, -94.25) * mm, "end": v(-15, -104.25) * mm});
            skLineSegment(sketch, "E92.MirrorCS", {"start": v(-35, -74.25) * mm, "end": v(-15, -94.25) * mm});
            skLineSegment(sketch, "E93.MirrorCS", {"start": v(35, -74.25) * mm, "end": v(15, -94.25) * mm});
            skLineSegment(sketch, "E94.MirrorCS", {"start": v(15, -104.25) * mm, "end": v(15, -94.25) * mm});
            skSolve(sketch);
        }
        {
            var Q0;
            Q0=makeQuery(id+"F16.imprint","IMPRINT",FACE,{"disambiguationData":[TD([[makeQuery(id+"F16.imprint","IMPRINT",EDGE,{"derivedFrom":sQuery(id+"F16.wireOp",EDGE,"E79")}),1.0]])]});
            var Q1;
            {var subQ6=sQuery(id+"F16.wireOp",EDGE,"E79");Q1=makeQuery(id+"F16.imprint","IMPRINT",FACE,{"disambiguationData":[TD([[makeQuery(id+"F16.imprint","IMPRINT",EDGE,{"derivedFrom":subQ6}),-1.0]])]});}
            var Q2;
            Q2=makeQuery(id+"F16.imprint","IMPRINT",FACE,{"disambiguationData":[TD([[makeQuery(id+"F16.imprint","IMPRINT",EDGE,{"derivedFrom":sQuery(id+"F16.wireOp",EDGE,"E89.MirrorCS")}),-1.0]])]});
            extrude(context, id + "F17", {"entities" : qUnion([Q0, Q1, Q2]), "depth" : 3 * mm});
        }
    });
